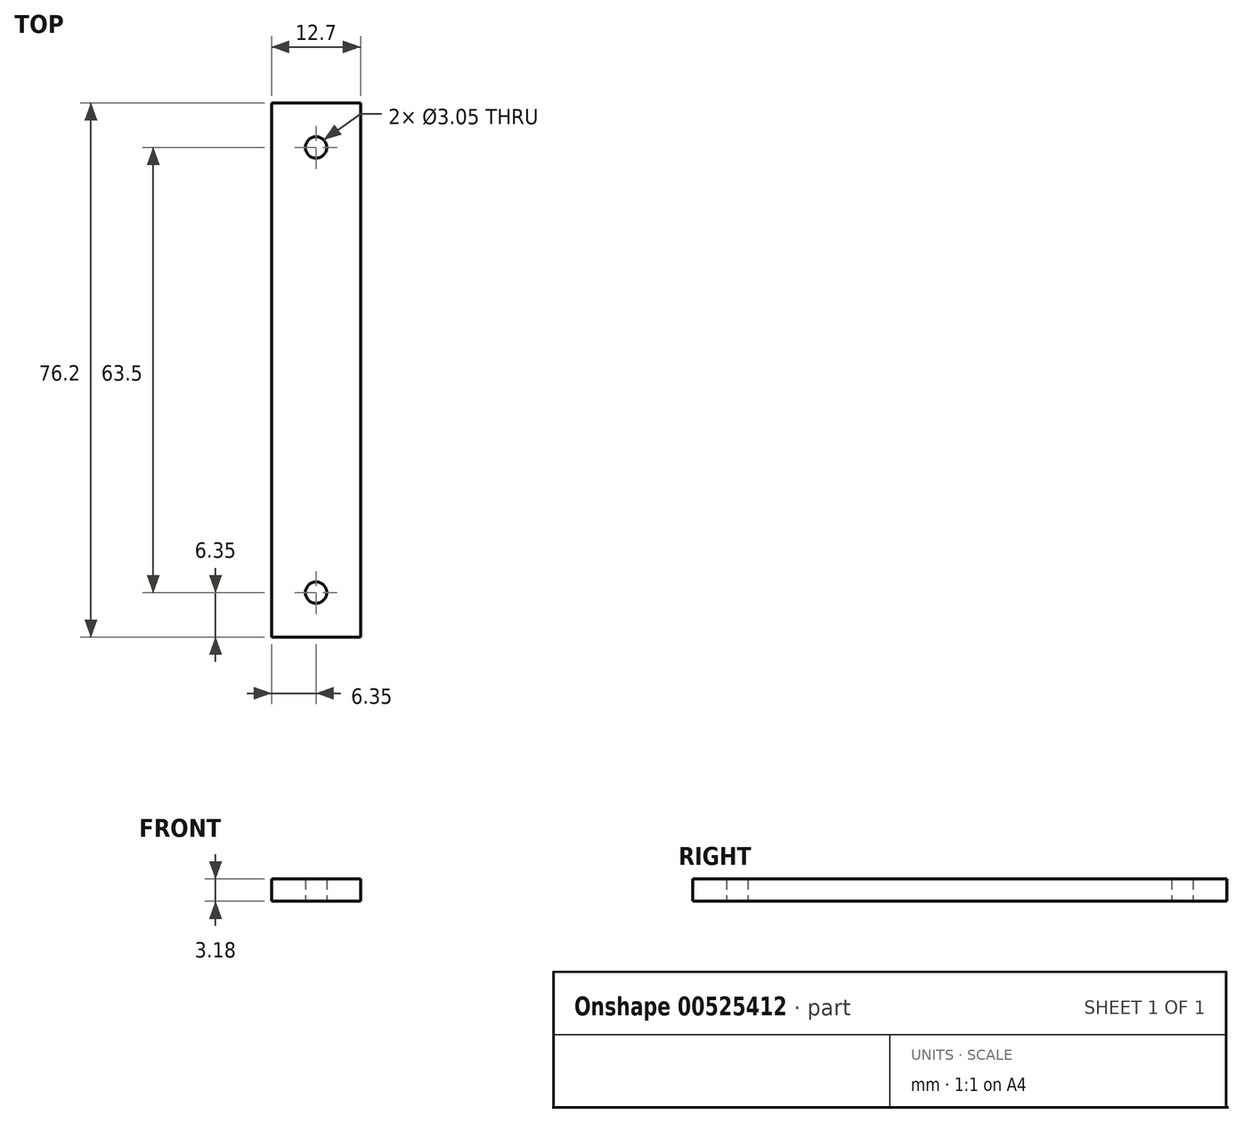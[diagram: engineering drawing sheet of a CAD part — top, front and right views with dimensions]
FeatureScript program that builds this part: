
annotation { "Feature Type Name" : "Feature", "Feature Type Description" : "" }
export const myFeature = defineFeature(function(context is Context, id is Id, definition is map)
    precondition{}
    {
        {
            var Q0;
            Q0=qCreatedBy(makeId("Top.planeOp"),FACE);
            var sketch = newSketch(context, id + "F0", { "sketchPlane" : qUnion([Q0])});
            skLineSegment(sketch, "E0.bottom", {"start": v(6.35, 38.1) * mm, "end": v(-6.35, 38.1) * mm});
            skLineSegment(sketch, "E0.top", {"start": v(6.35, -38.1) * mm, "end": v(-6.35, -38.1) * mm});
            skLineSegment(sketch, "E0.left", {"start": v(6.35, 38.1) * mm, "end": v(6.35, -38.1) * mm});
            skLineSegment(sketch, "E0.right", {"start": v(-6.35, 38.1) * mm, "end": v(-6.35, -38.1) * mm});
            skPoint(sketch, "E0.middle", {"position": v(0, 0) * mm});
            skCircle(sketch, "E1", {"center": v(0, -31.75) * mm, "radius": 1.52 * mm});
            skCircle(sketch, "E2.MirrorC", {"center": v(0, 31.75) * mm, "radius": 1.52 * mm});
            skSolve(sketch);
        }
        {
            var Q0;
            Q0=makeQuery(id+"F0.imprint","IMPRINT",FACE,{"disambiguationData":[TD([[makeQuery(id+"F0.imprint","IMPRINT",EDGE,{"derivedFrom":sQuery(id+"F0.wireOp",EDGE,"E0.bottom")}),1.0]])]});
            extrude(context, id + "F1", {"entities" : qUnion([Q0]), "depth" : 3.17 * mm, "offsetDistance" : 25.4 * mm});
        }
    });
